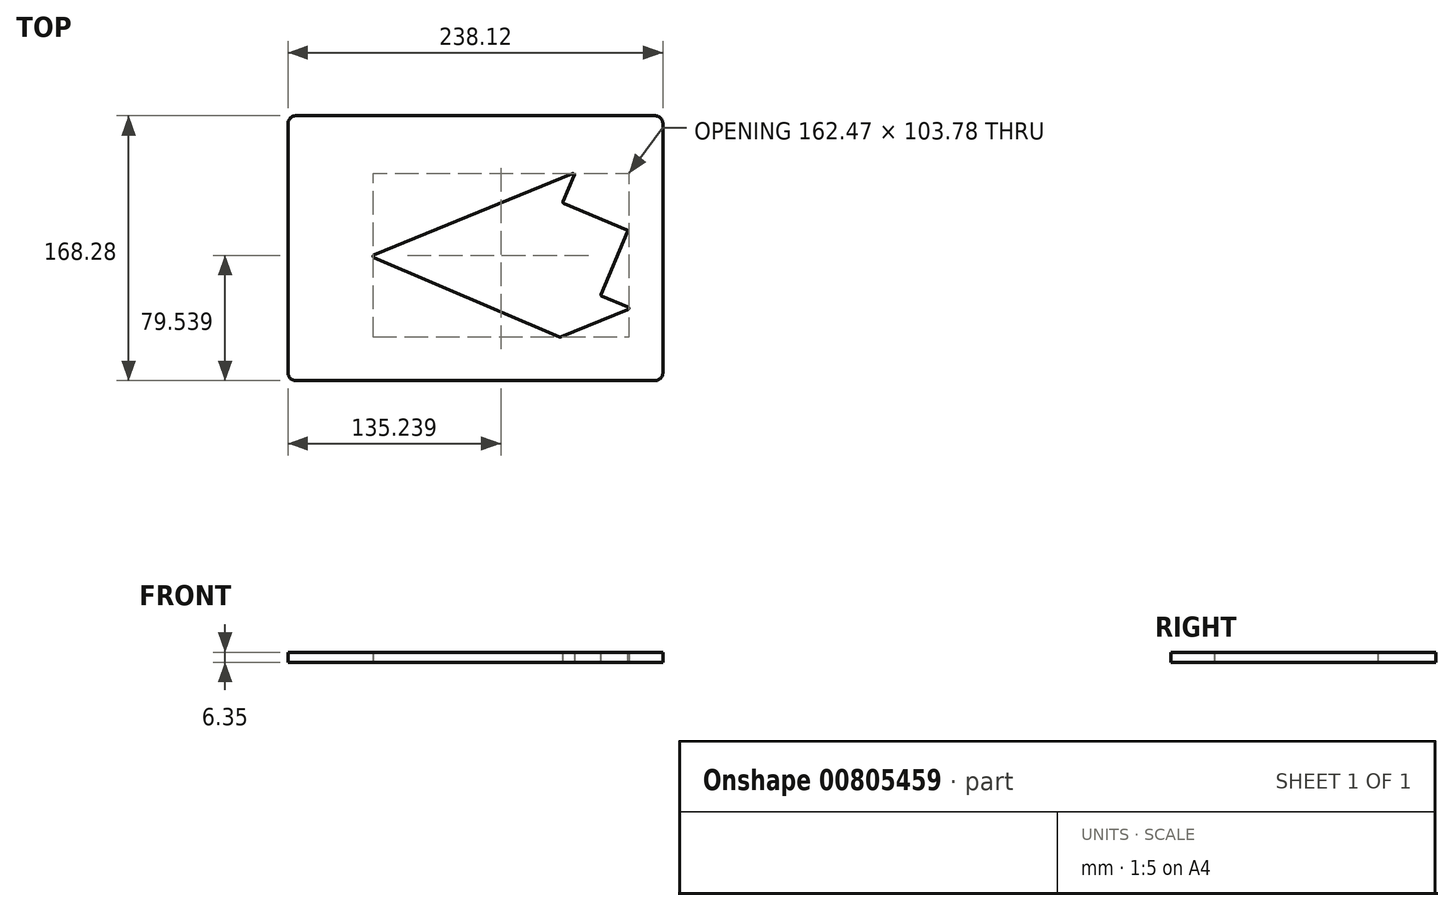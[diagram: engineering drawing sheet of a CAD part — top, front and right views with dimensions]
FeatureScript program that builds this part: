
annotation { "Feature Type Name" : "Feature", "Feature Type Description" : "" }
export const myFeature = defineFeature(function(context is Context, id is Id, definition is map)
    precondition{}
    {
        {
            var Q0;
            Q0=qCreatedBy(makeId("Top.planeOp"),FACE);
            var sketch = newSketch(context, id + "F0", { "sketchPlane" : qUnion([Q0])});
            skLineSegment(sketch, "E0.bottom", {"start": v(119.06, 84.14) * mm, "end": v(-119.06, 84.14) * mm});
            skLineSegment(sketch, "E0.top", {"start": v(119.06, -84.14) * mm, "end": v(-119.06, -84.14) * mm});
            skLineSegment(sketch, "E0.left", {"start": v(119.06, 84.14) * mm, "end": v(119.06, -84.14) * mm});
            skLineSegment(sketch, "E0.right", {"start": v(-119.06, 84.14) * mm, "end": v(-119.06, -84.14) * mm});
            skPoint(sketch, "E0.middle", {"position": v(0, 0) * mm});
            skSolve(sketch);
        }
        {
            var Q0;
            Q0 = qSketchRegion(id + "F0", true);
            extrude(context, id + "F1", {"entities" : qUnion([Q0]), "depth" : 6.35 * mm, "offsetDistance" : 25.4 * mm});
        }
        {
            var Q0;
            Q0=makeQuery(id+"F1.opExtrude","SWEPT_EDGE",EDGE,{"disambiguationData":[OSD([sQuery(id+"F0.wireOp",EDGE,"E0.bottom"),sQuery(id+"F0.wireOp",EDGE,"E0.right")])]});
            var Q1;
            Q1=makeQuery(id+"F1.opExtrude","SWEPT_EDGE",EDGE,{"disambiguationData":[OSD([sQuery(id+"F0.wireOp",EDGE,"E0.top"),sQuery(id+"F0.wireOp",EDGE,"E0.right")])]});
            var Q2;
            Q2=makeQuery(id+"F1.opExtrude","SWEPT_EDGE",EDGE,{"disambiguationData":[OSD([sQuery(id+"F0.wireOp",EDGE,"E0.bottom"),sQuery(id+"F0.wireOp",EDGE,"E0.left")])]});
            var Q3;
            Q3=makeQuery(id+"F1.opExtrude","SWEPT_EDGE",EDGE,{"disambiguationData":[OSD([sQuery(id+"F0.wireOp",EDGE,"E0.top"),sQuery(id+"F0.wireOp",EDGE,"E0.left")])]});
            fillet(context, id + "F2", {"entities" : qUnion([Q0, Q1, Q2, Q3]), "radius" : 5.08 * mm, "tangentPropagation" : true, "allowEdgeOverflow" : false});
        }
        {
            var Q0;
            Q0=makeQuery(id+"F1.opExtrude","CAP_FACE",FACE,{"disambiguationData":[OSD([sQuery(id+"F0.wireOp",EDGE,"E0.bottom"),sQuery(id+"F0.wireOp",EDGE,"E0.top"),sQuery(id+"F0.wireOp",EDGE,"E0.left"),sQuery(id+"F0.wireOp",EDGE,"E0.right")])],"isStart":false});
            var sketch = newSketch(context, id + "F3", { "sketchPlane" : qUnion([Q0])});
            skLineSegment(sketch, "E1", {"start": v(53.75, -55.18) * mm, "end": v(95.37, -38.17) * mm});
            skLineSegment(sketch, "E2", {"start": v(95.37, -38.17) * mm, "end": v(77.8, -30.8) * mm});
            skLineSegment(sketch, "E3", {"start": v(77.8, -30.8) * mm, "end": v(95.2, 10.65) * mm});
            skLineSegment(sketch, "E4", {"start": v(95.2, 10.65) * mm, "end": v(53.75, 28.05) * mm});
            skLineSegment(sketch, "E5", {"start": v(53.75, 28.05) * mm, "end": v(61.12, 45.62) * mm});
            skLineSegment(sketch, "E6", {"start": v(61.12, 45.62) * mm, "end": v(-63.02, -5.11) * mm});
            skLineSegment(sketch, "E7", {"start": v(-63.02, -5.11) * mm, "end": v(53.75, -55.18) * mm});
            skSolve(sketch);
        }
        {
            var Q0;
            Q0 = qSketchRegion(id + "F3", true);
            extrude(context, id + "F4", {"entities" : qUnion([Q0]), "operationType" : NewBodyOperationType.REMOVE, "oppositeDirection" : true, "depth" : 25.4 * mm, "offsetDistance" : 25.4 * mm});
        }
        {
            var Q0;
            Q0=makeQuery(id+"F1.opExtrude","CAP_FACE",FACE,{"disambiguationData":[OSD([sQuery(id+"F0.wireOp",EDGE,"E0.bottom"),sQuery(id+"F0.wireOp",EDGE,"E0.top"),sQuery(id+"F0.wireOp",EDGE,"E0.left"),sQuery(id+"F0.wireOp",EDGE,"E0.right")])],"isStart":false});
            var sketch = newSketch(context, id + "F5", { "sketchPlane" : qUnion([Q0])});
            skLineSegment(sketch, "E8.0", {"start": v(63.48, 47.96) * mm, "end": v(-66.3, -5.09) * mm});
            skLineSegment(sketch, "E8.1", {"start": v(55.41, 28.73) * mm, "end": v(63.48, 47.96) * mm});
            skLineSegment(sketch, "E8.2", {"start": v(53.74, -56.56) * mm, "end": v(98.69, -38.2) * mm});
            skLineSegment(sketch, "E8.3", {"start": v(98.69, -38.2) * mm, "end": v(79.47, -30.12) * mm});
            skLineSegment(sketch, "E8.4", {"start": v(79.47, -30.12) * mm, "end": v(96.87, 11.33) * mm});
            skLineSegment(sketch, "E8.5", {"start": v(-66.3, -5.09) * mm, "end": v(53.74, -56.56) * mm});
            skLineSegment(sketch, "E8.6", {"start": v(96.87, 11.33) * mm, "end": v(55.41, 28.73) * mm});
            skSolve(sketch);
        }
        {
            var Q0;
            Q0 = qSketchRegion(id + "F5", true);
            var Q1;
            Q1=makeQuery(id+"F5.imprint","IMPRINT",FACE,{"disambiguationData":[TD([[makeQuery(id+"F5.imprint","IMPRINT",EDGE,{"derivedFrom":sQuery(id+"F5.wireOp",EDGE,"E8.0")}),1.0]])]});
            extrude(context, id + "F6", {"entities" : qUnion([Q0, Q1]), "operationType" : NewBodyOperationType.REMOVE, "oppositeDirection" : true, "depth" : 25.4 * mm, "offsetDistance" : 25.4 * mm});
        }
        {
            var Q0;
            Q0=makeQuery(id+"F6.boolean.opBoolean","COPY",EDGE,{"derivedFrom":makeQuery(id+"F6.opExtrude","SWEPT_EDGE",EDGE,{"disambiguationData":[OSD([sQuery(id+"F5.wireOp",EDGE,"E8.0"),sQuery(id+"F5.wireOp",EDGE,"E8.5")])]})});
            var Q1;
            Q1=makeQuery(id+"F6.boolean.opBoolean","COPY",EDGE,{"derivedFrom":makeQuery(id+"F6.opExtrude","SWEPT_EDGE",EDGE,{"disambiguationData":[OSD([sQuery(id+"F5.wireOp",EDGE,"E8.0"),sQuery(id+"F5.wireOp",EDGE,"E8.1")])]})});
            var Q2;
            Q2=makeQuery(id+"F6.boolean.opBoolean","COPY",EDGE,{"derivedFrom":makeQuery(id+"F6.opExtrude","SWEPT_EDGE",EDGE,{"disambiguationData":[OSD([sQuery(id+"F5.wireOp",EDGE,"E8.4"),sQuery(id+"F5.wireOp",EDGE,"E8.6")])]})});
            var Q3;
            Q3=makeQuery(id+"F6.boolean.opBoolean","COPY",EDGE,{"derivedFrom":makeQuery(id+"F6.opExtrude","SWEPT_EDGE",EDGE,{"disambiguationData":[OSD([sQuery(id+"F5.wireOp",EDGE,"E8.1"),sQuery(id+"F5.wireOp",EDGE,"E8.6")])]})});
            var Q4;
            Q4=makeQuery(id+"F6.boolean.opBoolean","COPY",EDGE,{"derivedFrom":makeQuery(id+"F6.opExtrude","SWEPT_EDGE",EDGE,{"disambiguationData":[OSD([sQuery(id+"F5.wireOp",EDGE,"E8.3"),sQuery(id+"F5.wireOp",EDGE,"E8.4")])]})});
            var Q5;
            Q5=makeQuery(id+"F6.boolean.opBoolean","COPY",EDGE,{"derivedFrom":makeQuery(id+"F6.opExtrude","SWEPT_EDGE",EDGE,{"disambiguationData":[OSD([sQuery(id+"F5.wireOp",EDGE,"E8.2"),sQuery(id+"F5.wireOp",EDGE,"E8.3")])]})});
            var Q6;
            Q6=makeQuery(id+"F6.boolean.opBoolean","COPY",EDGE,{"derivedFrom":makeQuery(id+"F6.opExtrude","SWEPT_EDGE",EDGE,{"disambiguationData":[OSD([sQuery(id+"F5.wireOp",EDGE,"E8.2"),sQuery(id+"F5.wireOp",EDGE,"E8.5")])]})});
            fillet(context, id + "F7", {"entities" : qUnion([Q0, Q1, Q2, Q3, Q4, Q5, Q6]), "radius" : 0.79 * mm, "tangentPropagation" : true, "allowEdgeOverflow" : false});
        }
    });
